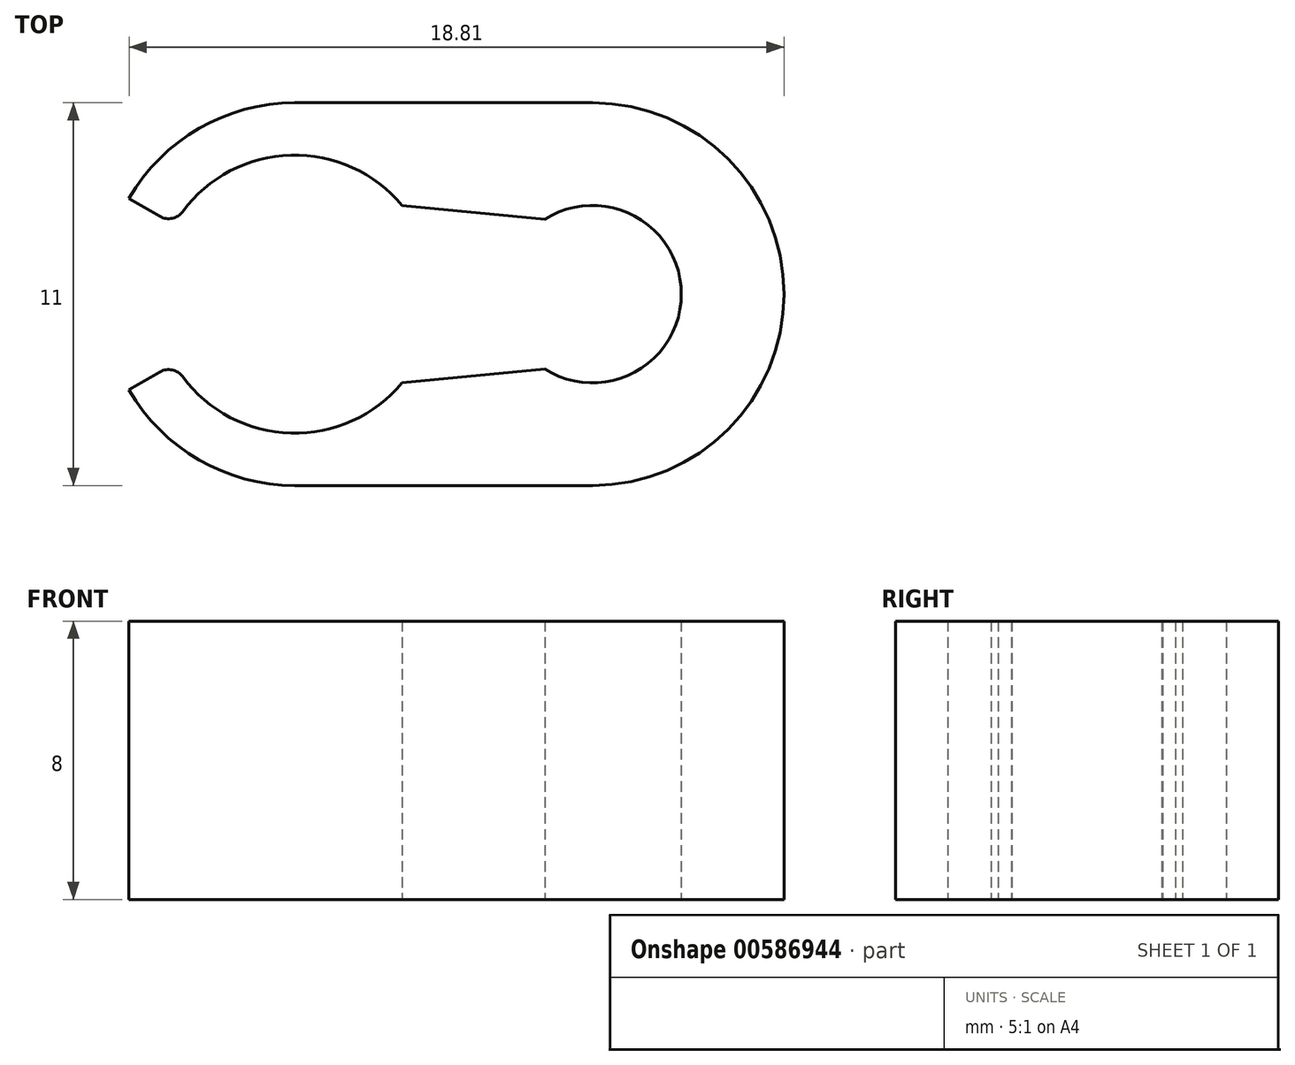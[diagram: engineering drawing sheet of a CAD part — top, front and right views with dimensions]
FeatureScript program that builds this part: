
annotation { "Feature Type Name" : "Feature", "Feature Type Description" : "" }
export const myFeature = defineFeature(function(context is Context, id is Id, definition is map)
    precondition{}
    {
        {
            var Q0;
            Q0=qCreatedBy(makeId("Top.planeOp"),FACE);
            var sketch = newSketch(context, id + "F0", { "sketchPlane" : qUnion([Q0])});
            skPoint(sketch, "E0", {"position": v(4, 0) * mm});
            skPoint(sketch, "E1", {"position": v(6, 0) * mm});
            skLineSegment(sketch, "E2", {"start": v(8.55, 2.55) * mm, "end": v(3.08, 2.55) * mm, "construction": true});
            skLineSegment(sketch, "E3", {"start": v(6, 0) * mm, "end": v(4, 0) * mm, "construction": true});
            skLineSegment(sketch, "E4.MirrorCS", {"start": v(8.55, -2.55) * mm, "end": v(3.08, -2.55) * mm, "construction": true});
            skArc(sketch, "E5", {"start": v(3.08, 2.55) * mm, "mid": v(-4, 0) * mm, "end": v(3.08, -2.55) * mm});
            skArc(sketch, "E6", {"start": v(3.08, -2.55) * mm, "mid": v(4, 0) * mm, "end": v(3.08, 2.55) * mm, "construction": true});
            skArc(sketch, "E7", {"start": v(8.55, 2.55) * mm, "mid": v(7.84, 2.45) * mm, "end": v(7.18, 2.15) * mm});
            skArc(sketch, "E8", {"start": v(8.55, -2.55) * mm, "mid": v(11.1, 0) * mm, "end": v(8.55, 2.55) * mm});
            skArc(sketch, "E9.0", {"start": v(3.72, 4.05) * mm, "mid": v(-5.5, 0) * mm, "end": v(3.72, -4.05) * mm});
            skLineSegment(sketch, "E9.1", {"start": v(8.55, 4.05) * mm, "end": v(3.72, 4.05) * mm});
            skArc(sketch, "E9.2", {"start": v(8.55, -4.05) * mm, "mid": v(12.6, 0) * mm, "end": v(8.55, 4.05) * mm});
            skLineSegment(sketch, "E9.3", {"start": v(8.55, -4.05) * mm, "end": v(3.72, -4.05) * mm});
            skLineSegment(sketch, "E10", {"start": v(3.08, 2.55) * mm, "end": v(7.18, 2.15) * mm});
            skArc(sketch, "E11", {"start": v(7.18, 2.15) * mm, "mid": v(6, 0) * mm, "end": v(7.18, -2.15) * mm, "construction": true});
            skLineSegment(sketch, "E12.MirrorCS", {"start": v(3.08, -2.55) * mm, "end": v(7.18, -2.15) * mm});
            skArc(sketch, "E13", {"start": v(7.18, -2.15) * mm, "mid": v(7.84, -2.45) * mm, "end": v(8.55, -2.55) * mm});
            skLineSegment(sketch, "E14", {"start": v(0, 0) * mm, "end": v(-4.76, 2.75) * mm});
            skLineSegment(sketch, "E15", {"start": v(0, 0) * mm, "end": v(0, 4) * mm, "construction": true});
            skLineSegment(sketch, "E16.MirrorCS", {"start": v(0, 0) * mm, "end": v(-4.76, -2.75) * mm});
            skLineSegment(sketch, "E17", {"start": v(0, 5.5) * mm, "end": v(8.55, 5.5) * mm});
            skLineSegment(sketch, "E18", {"start": v(0, -5.5) * mm, "end": v(8.55, -5.5) * mm});
            skArc(sketch, "E19", {"start": v(8.55, 5.5) * mm, "mid": v(14.05, 0) * mm, "end": v(8.55, -5.5) * mm});
            skSolve(sketch);
        }
        {
            var Q0;
            Q0=makeQuery(id+"F0.imprint","IMPRINT",FACE,{"disambiguationData":[TD([[makeQuery(id+"F0.imprint","IMPRINT",EDGE,{"derivedFrom":sQuery(id+"F0.wireOp",EDGE,"E7")}),-1.0]])]});
            var Q1;
            {var subQ4=sQuery(id+"F0.wireOp",EDGE,"E9.1");Q1=makeQuery(id+"F0.imprint","IMPRINT",FACE,{"disambiguationData":[TD([[makeQuery(id+"F0.imprint","IMPRINT",EDGE,{"derivedFrom":subQ4}),-1.0]])]});}
            extrude(context, id + "F1", {"entities" : qUnion([Q0, Q1]), "depth" : 8 * mm, "offsetDistance" : 25 * mm});
        }
        {
            var Q0;
            Q0=makeQuery(id+"F1.opExtrude","SWEPT_EDGE",EDGE,{"disambiguationData":[OSD([sQuery(id+"F0.wireOp",EDGE,"E5"),sQuery(id+"F0.wireOp",EDGE,"E16.MirrorCS")])]});
            var Q1;
            Q1=makeQuery(id+"F1.opExtrude","SWEPT_EDGE",EDGE,{"disambiguationData":[OSD([sQuery(id+"F0.wireOp",EDGE,"E5"),sQuery(id+"F0.wireOp",EDGE,"E14")])]});
            fillet(context, id + "F2", {"entities" : qUnion([Q0, Q1]), "radius" : .5 * mm, "tangentPropagation" : true, "allowEdgeOverflow" : false});
        }
    });
